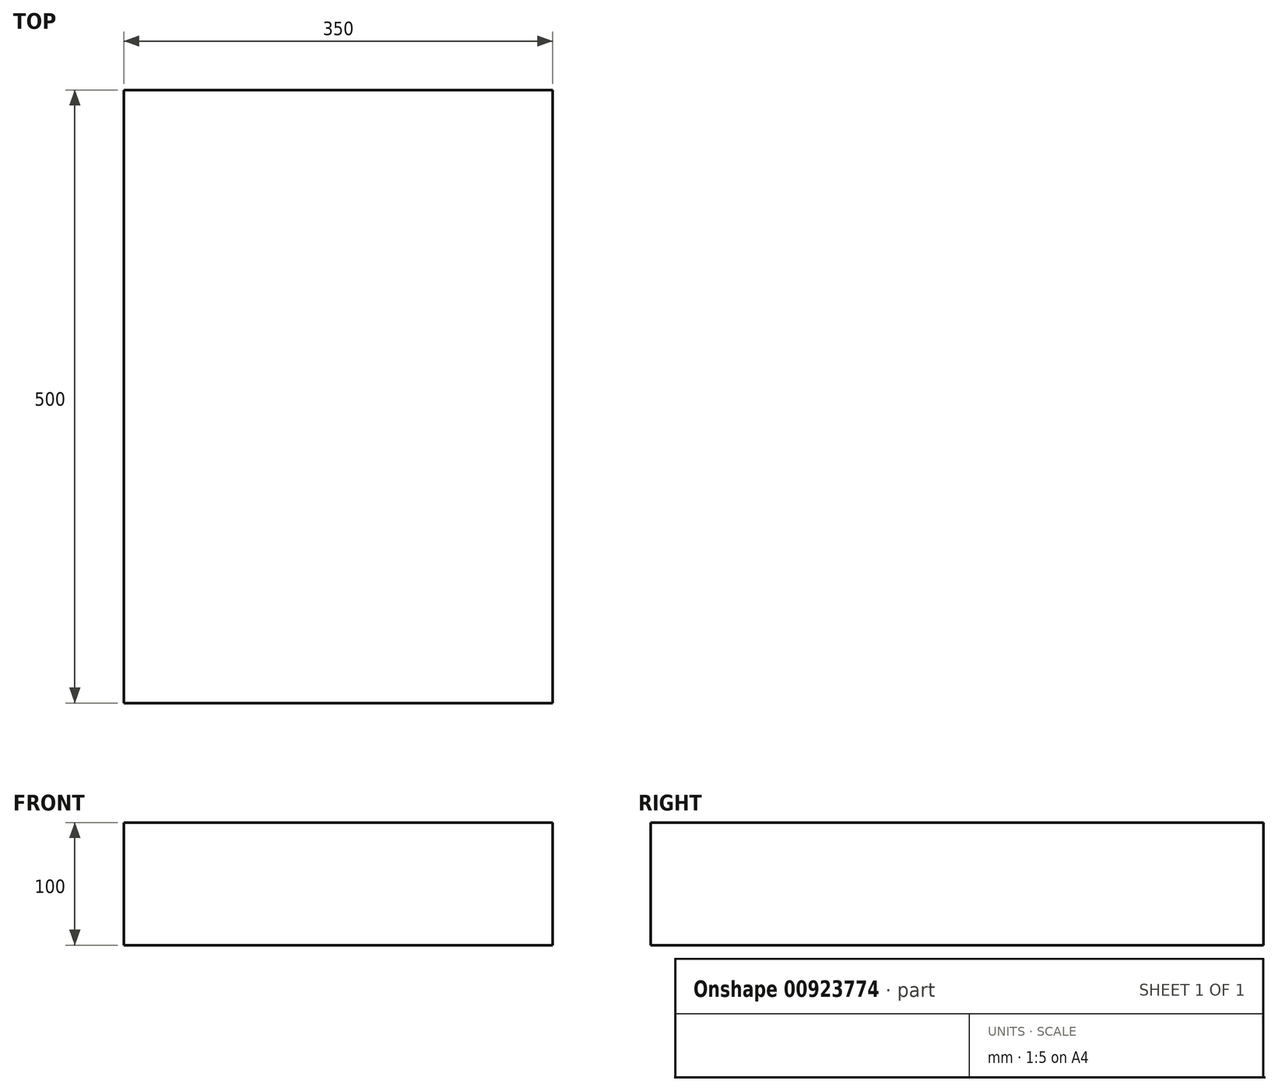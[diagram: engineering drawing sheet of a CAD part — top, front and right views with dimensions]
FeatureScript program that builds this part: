
annotation { "Feature Type Name" : "Feature", "Feature Type Description" : "" }
export const myFeature = defineFeature(function(context is Context, id is Id, definition is map)
    precondition{}
    {
        {
            var Q0;
            Q0=qCreatedBy(makeId("Top.planeOp"),FACE);
            var sketch = newSketch(context, id + "F0", { "sketchPlane" : qUnion([Q0])});
            skLineSegment(sketch, "E0", {"start": v(-144.63, -199.15) * mm, "end": v(-144.63, 300.85) * mm});
            skLineSegment(sketch, "E1", {"start": v(-494.63, 300.85) * mm, "end": v(-144.63, 300.85) * mm});
            skLineSegment(sketch, "E2", {"start": v(-494.63, 300.85) * mm, "end": v(-494.63, -199.15) * mm});
            skLineSegment(sketch, "E3", {"start": v(-494.63, -199.15) * mm, "end": v(-144.63, -199.15) * mm});
            skSolve(sketch);
        }
        {
            var Q0;
            Q0 = qSketchRegion(id + "F0", true);
            extrude(context, id + "F1", {"entities" : qUnion([Q0]), "depth" : 100 * mm, "offsetDistance" : 25 * mm});
        }
    });
